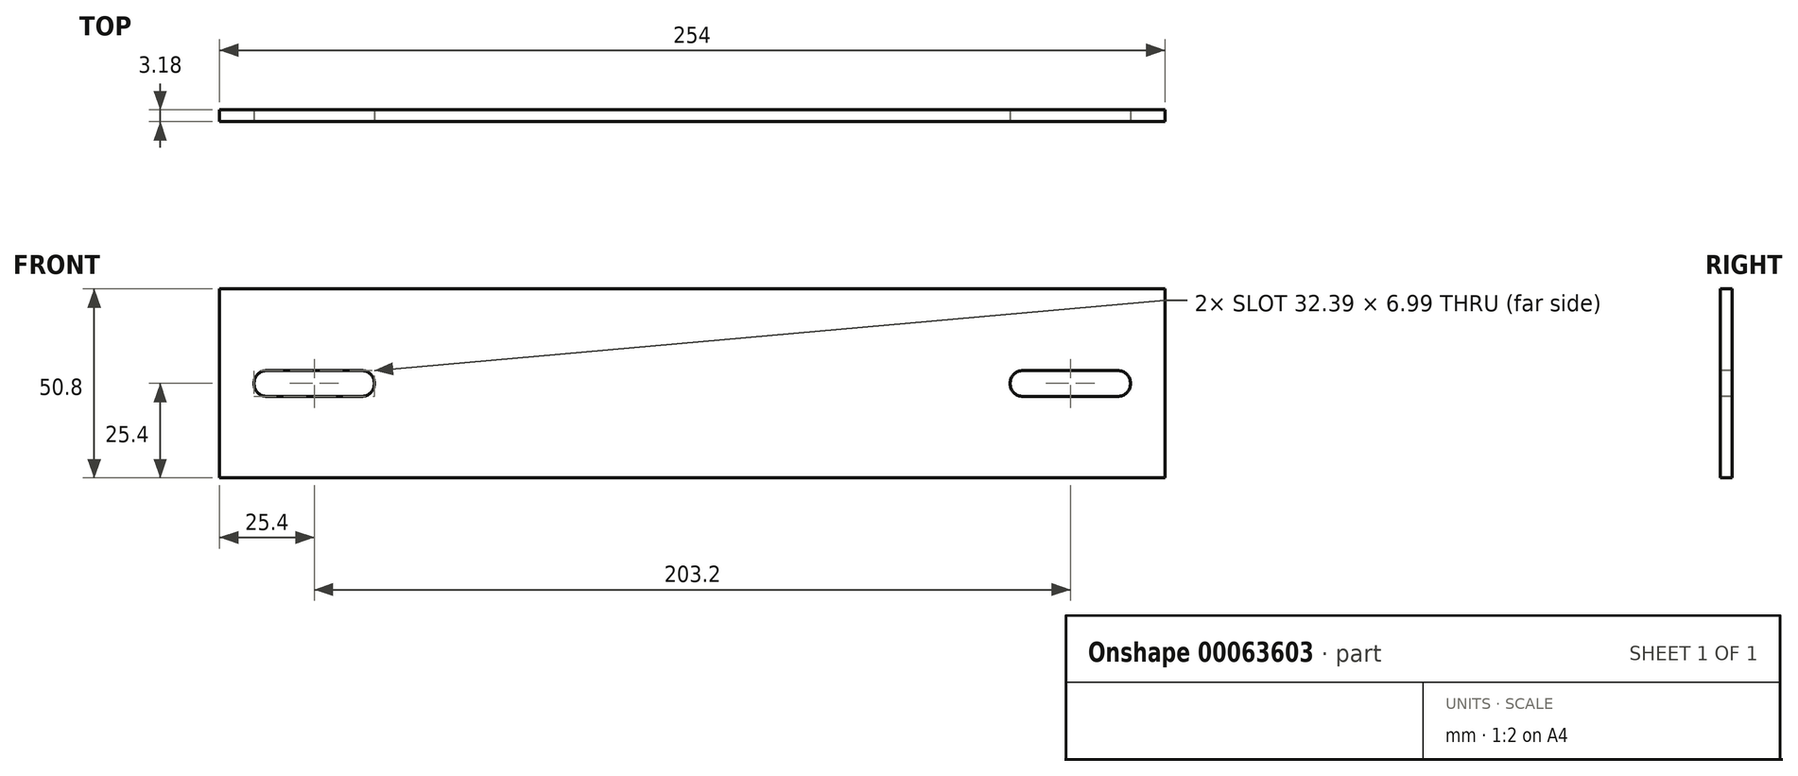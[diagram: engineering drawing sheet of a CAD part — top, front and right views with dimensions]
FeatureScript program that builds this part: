
annotation { "Feature Type Name" : "Feature", "Feature Type Description" : "" }
export const myFeature = defineFeature(function(context is Context, id is Id, definition is map)
    precondition{}
    {
        {
            var Q0;
            Q0=qCreatedBy(makeId("Front.planeOp"),FACE);
            var sketch = newSketch(context, id + "F0", { "sketchPlane" : qUnion([Q0])});
            skLineSegment(sketch, "E0.rect.bottom", {"start": v(127, -25.4) * mm, "end": v(-127, -25.4) * mm});
            skLineSegment(sketch, "E0.rect.top", {"start": v(127, 25.4) * mm, "end": v(-127, 25.4) * mm});
            skLineSegment(sketch, "E0.rect.left", {"start": v(127, -25.4) * mm, "end": v(127, 25.4) * mm});
            skLineSegment(sketch, "E0.rect.right", {"start": v(-127, -25.4) * mm, "end": v(-127, 25.4) * mm});
            skPoint(sketch, "E0.rect.middle", {"position": v(0, 0) * mm});
            skSolve(sketch);
        }
        {
            var Q0;
            Q0=makeQuery(id+"F0.imprint","IMPRINT",FACE,{"disambiguationData":[TD([[makeQuery(id+"F0.imprint","IMPRINT",EDGE,{"derivedFrom":sQuery(id+"F0.wireOp",EDGE,"E0.rect.bottom")}),-1.0]])]});
            extrude(context, id + "F1", {"entities" : qUnion([Q0]), "depth" : 3.17 * mm});
        }
        {
            var Q0;
            Q0=makeQuery(id+"F1.opExtrude","CAP_FACE",FACE,{"disambiguationData":[OSD([sQuery(id+"F0.wireOp",EDGE,"E0.rect.bottom"),sQuery(id+"F0.wireOp",EDGE,"E0.rect.top"),sQuery(id+"F0.wireOp",EDGE,"E0.rect.left"),sQuery(id+"F0.wireOp",EDGE,"E0.rect.right")])],"isStart":false});
            var sketch = newSketch(context, id + "F2", { "sketchPlane" : qUnion([Q0])});
            skArc(sketch, "E1", {"start": v(-114.3, 3.5) * mm, "mid": v(-117.8, 0) * mm, "end": v(-114.3, -3.5) * mm});
            skArc(sketch, "E2", {"start": v(-88.9, -3.5) * mm, "mid": v(-85.4, 0) * mm, "end": v(-88.9, 3.5) * mm});
            skLineSegment(sketch, "E3", {"start": v(-114.3, 3.5) * mm, "end": v(-88.9, 3.5) * mm});
            skLineSegment(sketch, "E4", {"start": v(-114.3, -3.5) * mm, "end": v(-88.9, -3.5) * mm});
            skLineSegment(sketch, "E5.MirrorCS", {"start": v(114.3, -3.5) * mm, "end": v(88.9, -3.5) * mm});
            skLineSegment(sketch, "E6.MirrorCS", {"start": v(114.3, 3.5) * mm, "end": v(88.9, 3.5) * mm});
            skArc(sketch, "E7.MirrorCS", {"start": v(88.9, -3.5) * mm, "mid": v(85.4, 0) * mm, "end": v(88.9, 3.5) * mm});
            skArc(sketch, "E8.MirrorCS", {"start": v(114.3, 3.5) * mm, "mid": v(117.8, 0) * mm, "end": v(114.3, -3.5) * mm});
            skSolve(sketch);
        }
        {
            var Q0;
            Q0 = qSketchRegion(id + "F2", true);
            extrude(context, id + "F3", {"entities" : qUnion([Q0]), "operationType" : NewBodyOperationType.REMOVE, "oppositeDirection" : true, "depth" : 25.4 * mm});
        }
    });
